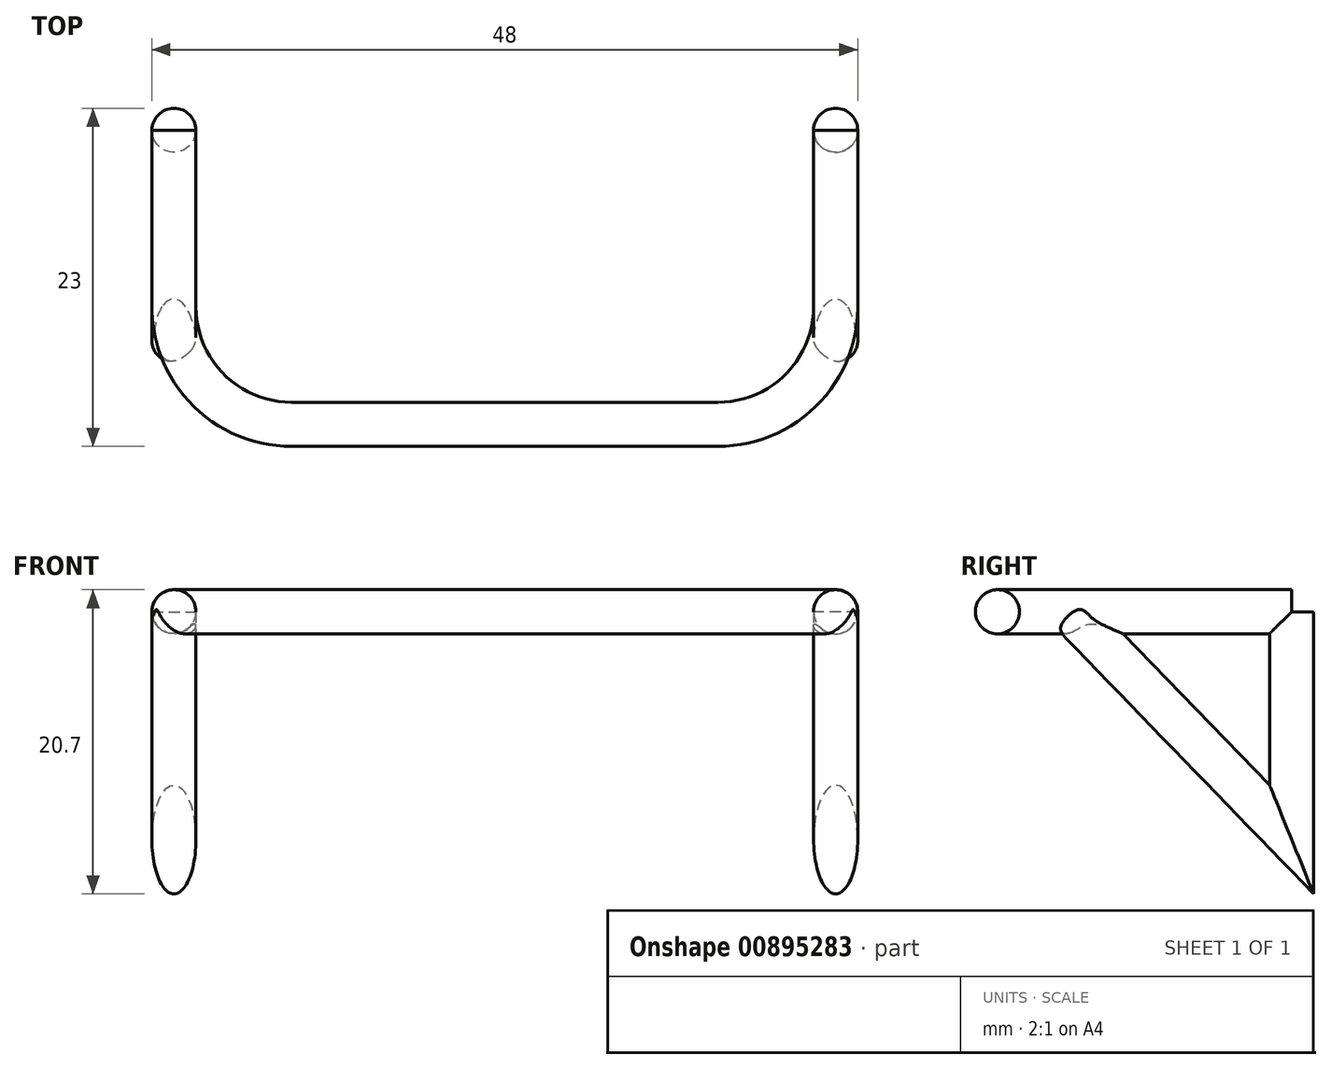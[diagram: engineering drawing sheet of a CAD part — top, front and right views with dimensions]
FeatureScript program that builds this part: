
annotation { "Feature Type Name" : "Feature", "Feature Type Description" : "" }
export const myFeature = defineFeature(function(context is Context, id is Id, definition is map)
    precondition{}
    {
        {
            var Q0;
            Q0=qCreatedBy(makeId("Top.planeOp"),FACE);
            var sketch = newSketch(context, id + "F0", { "sketchPlane" : qUnion([Q0])});
            skLineSegment(sketch, "E0", {"start": v(-45, 0) * mm, "end": v(-45, -12) * mm});
            skLineSegment(sketch, "E1", {"start": v(-37, -20) * mm, "end": v(-8, -20) * mm});
            skLineSegment(sketch, "E2", {"start": v(0, -12) * mm, "end": v(0, 0) * mm});
            skPoint(sketch, "E3.visualSharp", {"position": v(-45, -20) * mm});
            skArc(sketch, "E3.filletArc", {"start": v(-45, -12) * mm, "mid": v(-42.66, -17.66) * mm, "end": v(-37, -20) * mm});
            skPoint(sketch, "E4.visualSharp", {"position": v(0, -20) * mm});
            skArc(sketch, "E4.filletArc", {"start": v(-8, -20) * mm, "mid": v(-2.34, -17.66) * mm, "end": v(0, -12) * mm});
            skSolve(sketch);
        }
        {
            var Q0;
            Q0=qCreatedBy(makeId("Front.planeOp"),FACE);
            var sketch = newSketch(context, id + "F1", { "sketchPlane" : qUnion([Q0])});
            skCircle(sketch, "E5", {"center": v(0, 0) * mm, "radius": 1.5 * mm});
            skSolve(sketch);
        }
        {
            var Q0;
            Q0=makeQuery(id+"F1.imprint","IMPRINT",FACE,{"disambiguationData":[TD([[makeQuery(id+"F1.imprint","IMPRINT",EDGE,{"derivedFrom":sQuery(id+"F1.wireOp",EDGE,"E5")}),1.0]])]});
            var Q1;
            Q1=sQuery(id+"F0.wireOp",EDGE,"E2");
            var Q2;
            Q2=sQuery(id+"F0.wireOp",EDGE,"E4.filletArc");
            var Q3;
            Q3=sQuery(id+"F0.wireOp",EDGE,"E1");
            var Q4;
            Q4=sQuery(id+"F0.wireOp",EDGE,"E3.filletArc");
            var Q5;
            Q5=sQuery(id+"F0.wireOp",EDGE,"E0");
            sweep(context, id + "F2", {"profiles" : qUnion([Q0]), "path" : qUnion([Q1, Q2, Q3, Q4, Q5])});
        }
        {
            var Q0;
            Q0=qCreatedBy(makeId("Right.planeOp"),FACE);
            var sketch = newSketch(context, id + "F3", { "sketchPlane" : qUnion([Q0])});
            skLineSegment(sketch, "E6", {"start": v(-15, 0) * mm, "end": v(0, -15.5) * mm});
            skLineSegment(sketch, "E7", {"start": v(0, 0) * mm, "end": v(0, -15.5) * mm});
            skSolve(sketch);
        }
        {
            var Q0;
            Q0=qCreatedBy(makeId("Top.planeOp"),FACE);
            var sketch = newSketch(context, id + "F4", { "sketchPlane" : qUnion([Q0])});
            skCircle(sketch, "E8", {"center": v(0, 0) * mm, "radius": 1.5 * mm});
            skSolve(sketch);
        }
        {
            var Q0;
            Q0=makeQuery(id+"F4.imprint","IMPRINT",FACE,{"disambiguationData":[TD([[makeQuery(id+"F4.imprint","IMPRINT",EDGE,{"derivedFrom":sQuery(id+"F4.wireOp",EDGE,"E8")}),1.0]])]});
            var Q1;
            Q1=sQuery(id+"F3.wireOp",EDGE,"E7");
            var Q2;
            Q2=sQuery(id+"F3.wireOp",EDGE,"E6");
            sweep(context, id + "F5", {"operationType" : NewBodyOperationType.ADD, "profiles" : qUnion([Q0]), "path" : qUnion([Q1, Q2])});
        }
        {
            var Q0;
            Q0=makeQuery(id+"F5.opSweep","CAP_EDGE",EDGE,{"disambiguationData":[OSD([sQuery(id+"F3.wireOp",VERTEX,"E6.start"),sQuery(id+"F4.wireOp",EDGE,"E8")])],"isStart":false});
            fillet(context, id + "F6", {"entities" : qUnion([Q0]), "radius" : 1 * mm, "rho" : 0.5, "crossSection" : FilletCrossSection.CONIC, "allowEdgeOverflow" : false});
        }
        {
            var Q0;
            Q0=qCreatedBy(makeId("Right.planeOp"),FACE);
            cPlane(context, id + "F7", {"entities" : qUnion([Q0]), "cplaneType" : CPlaneType.OFFSET, "offset" : 45 * mm, "oppositeDirection" : true, "width" : 150 * mm, "height" : 150 * mm});
        }
        {
            var Q0;
            Q0=qCreatedBy(id+"F7.planeOp",FACE);
            cPlane(context, id + "F8", {"entities" : qUnion([Q0]), "cplaneType" : CPlaneType.OFFSET, "offset" : 22.5 * mm, "width" : 150 * mm, "height" : 150 * mm});
        }
        {
            var Q0;
            Q0=makeQuery(id+"F2.opSweep","SWEPT_BODY",BODY,{"disambiguationData":[OSD([sQuery(id+"F0.wireOp",EDGE,"E0"),sQuery(id+"F1.wireOp",EDGE,"E5")])]});
            var Q1;
            Q1=qCreatedBy(id+"F8.planeOp",FACE);
            mirror(context, id + "F9", {"operationType" : NewBodyOperationType.ADD, "entities" : qUnion([Q0]), "mirrorPlane" : qUnion([Q1])});
        }
    });
